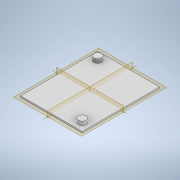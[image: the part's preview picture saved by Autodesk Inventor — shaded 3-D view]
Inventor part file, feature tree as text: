
AUTODESK INVENTOR PART (.ipt)
format: ipt  version: 2022.4 (Build 264492010, 492A)  size: 112,128 bytes
history: native  units: mm
features: extrude x2, sketch x2
ambient origin geometry x8: Origin, YZ Plane, XZ Plane, XY Plane, X Axis, Y Axis, Z Axis, Center Point
bodies: Solid1 (feature_tree)
feature tree (4):
  extrude  "Extrusion1"  Depth=50.0mm
  extrude  "Extrusion2"  Depth=2.5mm
  sketch  "Sketch1"  dims[d0=40.0mm d1=50.0mm]
  sketch  "Sketch2"  dims[d2=1.0mm d3=0.0mm d4=5.0mm d5=5.0mm d6=5.0mm d7=20.0mm d9=360.0deg d11=2.5mm d12=0.0mm]
